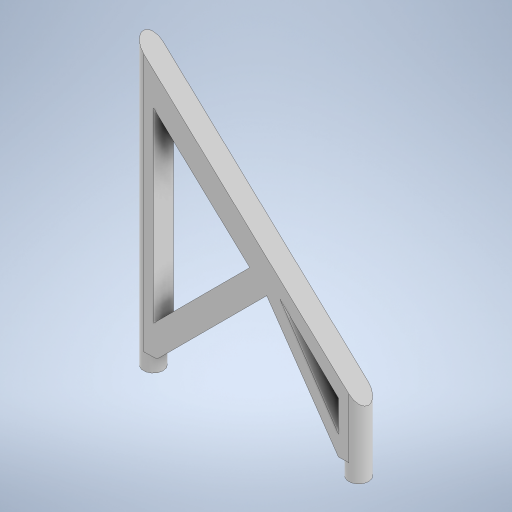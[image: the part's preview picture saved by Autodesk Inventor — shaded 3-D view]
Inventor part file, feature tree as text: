
AUTODESK INVENTOR PART (.ipt)
format: ipt  version: 2024 (Build 280153000, 153)  size: 304,128 bytes
history: native  units: mm
features: extrude x4, sketch x4, plane x1
ambient origin geometry x8: Origin, YZ Plane, XZ Plane, XY Plane, X Axis, Y Axis, Z Axis, Center Point
bodies: Solid1 (feature_tree)
feature tree (9):
  extrude  "Extrusion1"  Depth=3.0mm
  extrude  "Extrusion2"  Depth=3.0mm
  plane  "Work Plane1"
  extrude  "Extrusion3"  Depth=1.0mm
  extrude  "Extrusion4"  Depth=51.0mm
  sketch  "Sketch1"  dims[d0=3.0mm d1=3.0mm]
  sketch  "Sketch2"  dims[d2=3.0mm d3=3.0mm]
  sketch  "Sketch3"  dims[d5=49.0mm d6=1.0mm]
  sketch  "Sketch4"  dims[d7=30.0mm d8=51.0mm d9=2.5mm d10=0.0mm d11=45.0mm d12=0.0mm d13=2.0mm d14=45.0deg d15=10.0mm d16=45.0mm d17=0.0mm d18=3.5mm d19=3.5mm d20=3.5mm d21=3.5mm d22=45.0deg d23=3.0mm d24=1.8mm d25=3.0mm d26=2.0mm d27=12.283116mm d28=3.0mm d29=43.0mm d30=10.0mm d31=0.0mm]
